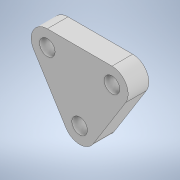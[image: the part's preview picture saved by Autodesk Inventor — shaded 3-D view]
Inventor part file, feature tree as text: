
AUTODESK INVENTOR PART (.ipt)
format: ipt  version: 2020 (Build 240168000, 168)  size: 113,152 bytes
history: native  units: mm
features: extrude x1, sketch x1
ambient origin geometry x8: Origin, YZ Plane, XZ Plane, XY Plane, X Axis, Y Axis, Z Axis, Center Point
bodies: Solid1 (feature_tree)
feature tree (2):
  extrude  "Extrusion1"  Depth=1.6mm
  sketch  "Sketch1"  dims[d0=5.0mm d1=2.5mm d2=4.0mm d3=1.2mm d4=1.6mm d5=0.0mm]
